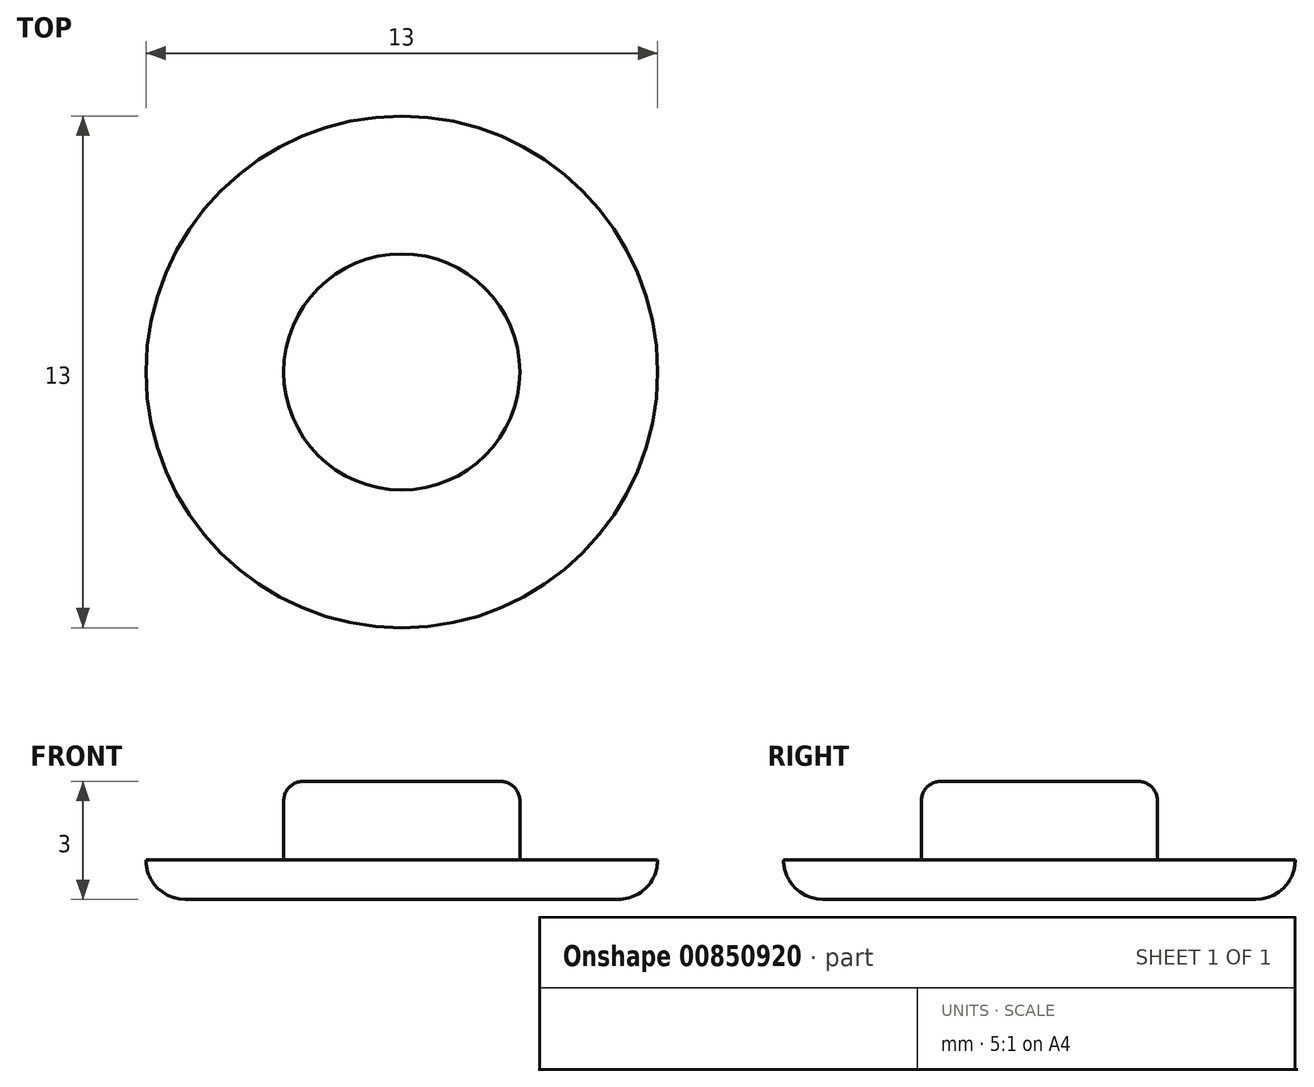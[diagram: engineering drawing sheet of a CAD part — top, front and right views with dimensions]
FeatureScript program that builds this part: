
annotation { "Feature Type Name" : "Feature", "Feature Type Description" : "" }
export const myFeature = defineFeature(function(context is Context, id is Id, definition is map)
    precondition{}
    {
        {
            var Q0;
            Q0=qCreatedBy(makeId("Top.planeOp"),FACE);
            var sketch = newSketch(context, id + "F0", { "sketchPlane" : qUnion([Q0])});
            skCircle(sketch, "E0", {"center": v(0, 0) * mm, "radius": 3 * mm});
            skCircle(sketch, "E1", {"center": v(0, 0) * mm, "radius": 6.5 * mm});
            skSolve(sketch);
        }
        {
            var Q0;
            Q0=makeQuery(id+"F0.imprint","IMPRINT",FACE,{"disambiguationData":[TD([[makeQuery(id+"F0.imprint","IMPRINT",EDGE,{"derivedFrom":sQuery(id+"F0.wireOp",EDGE,"E0")}),-1.0]])]});
            extrude(context, id + "F1", {"entities" : qUnion([Q0]), "depth" : 1 * mm, "offsetDistance" : 25 * mm});
        }
        {
            var Q0;
            Q0=makeQuery(id+"F0.imprint","IMPRINT",FACE,{"disambiguationData":[TD([[makeQuery(id+"F0.imprint","IMPRINT",EDGE,{"derivedFrom":sQuery(id+"F0.wireOp",EDGE,"E0")}),1.0]])]});
            extrude(context, id + "F2", {"entities" : qUnion([Q0]), "operationType" : NewBodyOperationType.ADD, "depth" : 3 * mm, "offsetDistance" : 25 * mm});
        }
        {
            var Q0;
            Q0=makeQuery(id+"F1.opExtrude","CAP_EDGE",EDGE,{"disambiguationData":[OSD([sQuery(id+"F0.wireOp",EDGE,"E1")])],"isStart":true});
            fillet(context, id + "F3", {"entities" : qUnion([Q0]), "radius" : 1 * mm, "tangentPropagation" : true, "allowEdgeOverflow" : false});
        }
        {
            var Q0;
            Q0=makeQuery(id+"F2.opExtrude","CAP_EDGE",EDGE,{"disambiguationData":[OSD([sQuery(id+"F0.wireOp",EDGE,"E0")])],"isStart":false});
            fillet(context, id + "F4", {"entities" : qUnion([Q0]), "radius" : .5 * mm, "tangentPropagation" : true, "allowEdgeOverflow" : false});
        }
    });
